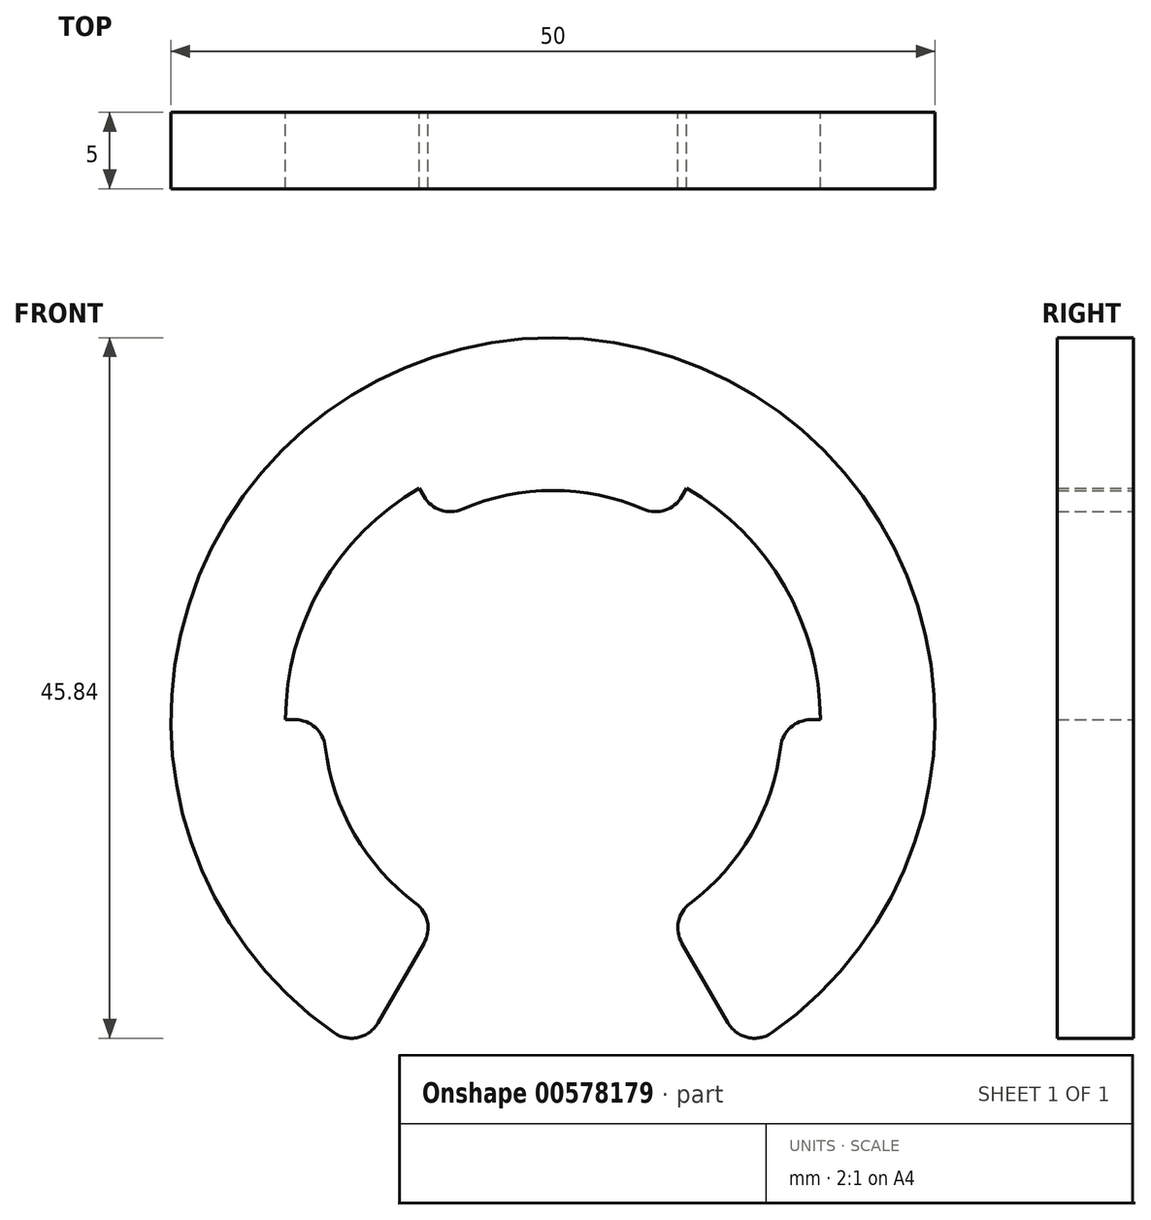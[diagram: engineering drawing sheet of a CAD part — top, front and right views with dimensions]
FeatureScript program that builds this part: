
annotation { "Feature Type Name" : "Feature", "Feature Type Description" : "" }
export const myFeature = defineFeature(function(context is Context, id is Id, definition is map)
    precondition{}
    {
        {
            var Q0;
            Q0=qCreatedBy(makeId("Front.planeOp"),FACE);
            var sketch = newSketch(context, id + "F0", { "sketchPlane" : qUnion([Q0])});
            skArc(sketch, "E0", {"start": v(12.5, -21.65) * mm, "mid": v(0, 25) * mm, "end": v(-12.5, -21.65) * mm});
            skArc(sketch, "E1", {"start": v(8.75, -15.16) * mm, "mid": v(0, 17.5) * mm, "end": v(-8.75, -15.16) * mm});
            skLineSegment(sketch, "E2", {"start": v(7.5, 13) * mm, "end": v(12.5, 21.65) * mm});
            skLineSegment(sketch, "E3", {"start": v(-7.5, 13) * mm, "end": v(-12.5, 21.65) * mm});
            skLineSegment(sketch, "E4", {"start": v(-15, 0) * mm, "end": v(-25, 0) * mm});
            skLineSegment(sketch, "E5", {"start": v(15, 0) * mm, "end": v(25, 0) * mm});
            skLineSegment(sketch, "E6", {"start": v(7.5, -13) * mm, "end": v(12.5, -21.65) * mm});
            skLineSegment(sketch, "E7", {"start": v(-7.5, -13) * mm, "end": v(-12.5, -21.65) * mm});
            skArc(sketch, "E8", {"start": v(7.5, -13) * mm, "mid": v(13, -7.5) * mm, "end": v(15, 0) * mm});
            skArc(sketch, "E9.trimOffspring", {"start": v(-15, 0) * mm, "mid": v(-13, -7.5) * mm, "end": v(-7.5, -13) * mm});
            skArc(sketch, "E10.trimOffspring", {"start": v(7.5, 13) * mm, "mid": v(0, 15) * mm, "end": v(-7.5, 13) * mm});
            skSolve(sketch);
        }
        {
            var Q0;
            {var subQ0=sQuery(id+"F0.wireOp",EDGE,"E3");var subQ1=sQuery(id+"F0.wireOp",EDGE,"E0");var subQ2=makeQuery(id+"F0.imprint","INTERSECT",VERTEX,{"derivedFrom":[subQ1,subQ0]});Q0=makeQuery(id+"F0.imprint","IMPRINT",FACE,{"disambiguationData":[TD([[makeQuery(id+"F0.imprint","IMPRINT",EDGE,{"disambiguationData":[TD([[subQ2,-1.0]])],"derivedFrom":subQ1}),1.0]])]});}
            var Q1;
            {var subQ0=sQuery(id+"F0.wireOp",EDGE,"E7");var subQ1=sQuery(id+"F0.wireOp",EDGE,"E0");var subQ2=makeQuery(id+"F0.imprint","INTERSECT",VERTEX,{"derivedFrom":[subQ1,subQ0]});Q1=makeQuery(id+"F0.imprint","IMPRINT",FACE,{"disambiguationData":[TD([[makeQuery(id+"F0.imprint","IMPRINT",EDGE,{"disambiguationData":[TD([[subQ2,1.0]])],"derivedFrom":subQ1}),1.0]])]});}
            var Q2;
            {var subQ5=sQuery(id+"F0.wireOp",EDGE,"E9.trimOffspring");Q2=makeQuery(id+"F0.imprint","IMPRINT",FACE,{"disambiguationData":[TD([[makeQuery(id+"F0.imprint","IMPRINT",EDGE,{"derivedFrom":subQ5}),-1.0]])]});}
            var Q3;
            {var subQ5=sQuery(id+"F0.wireOp",EDGE,"E10.trimOffspring");Q3=makeQuery(id+"F0.imprint","IMPRINT",FACE,{"disambiguationData":[TD([[makeQuery(id+"F0.imprint","IMPRINT",EDGE,{"derivedFrom":subQ5}),-1.0]])]});}
            var Q4;
            {var subQ0=sQuery(id+"F0.wireOp",EDGE,"E2");var subQ1=sQuery(id+"F0.wireOp",EDGE,"E0");var subQ2=makeQuery(id+"F0.imprint","INTERSECT",VERTEX,{"derivedFrom":[subQ1,subQ0]});Q4=makeQuery(id+"F0.imprint","IMPRINT",FACE,{"disambiguationData":[TD([[makeQuery(id+"F0.imprint","IMPRINT",EDGE,{"disambiguationData":[TD([[subQ2,-1.0]])],"derivedFrom":subQ1}),1.0]])]});}
            var Q5;
            {var subQ0=sQuery(id+"F0.wireOp",EDGE,"E2");var subQ1=sQuery(id+"F0.wireOp",EDGE,"E0");var subQ2=makeQuery(id+"F0.imprint","INTERSECT",VERTEX,{"derivedFrom":[subQ1,subQ0]});Q5=makeQuery(id+"F0.imprint","IMPRINT",FACE,{"disambiguationData":[TD([[makeQuery(id+"F0.imprint","IMPRINT",EDGE,{"disambiguationData":[TD([[subQ2,1.0]])],"derivedFrom":subQ1}),1.0]])]});}
            var Q6;
            {var subQ5=sQuery(id+"F0.wireOp",EDGE,"E8");Q6=makeQuery(id+"F0.imprint","IMPRINT",FACE,{"disambiguationData":[TD([[makeQuery(id+"F0.imprint","IMPRINT",EDGE,{"derivedFrom":subQ5}),-1.0]])]});}
            var Q7;
            {var subQ0=sQuery(id+"F0.wireOp",EDGE,"E6");var subQ1=sQuery(id+"F0.wireOp",EDGE,"E0");var subQ2=makeQuery(id+"F0.imprint","INTERSECT",VERTEX,{"derivedFrom":[subQ1,subQ0]});Q7=makeQuery(id+"F0.imprint","IMPRINT",FACE,{"disambiguationData":[TD([[makeQuery(id+"F0.imprint","IMPRINT",EDGE,{"disambiguationData":[TD([[subQ2,-1.0]])],"derivedFrom":subQ1}),1.0]])]});}
            extrude(context, id + "F1", {"entities" : qUnion([Q0, Q1, Q2, Q3, Q4, Q5, Q6, Q7]), "depth" : 5 * mm, "offsetDistance" : 25 * mm});
        }
        {
            var Q0;
            Q0=makeQuery(id+"F1.opExtrude","SWEPT_EDGE",EDGE,{"disambiguationData":[OSD([sQuery(id+"F0.wireOp",EDGE,"E2"),sQuery(id+"F0.wireOp",EDGE,"E10.trimOffspring")])]});
            var Q1;
            Q1=makeQuery(id+"F1.opExtrude","SWEPT_EDGE",EDGE,{"disambiguationData":[OSD([sQuery(id+"F0.wireOp",EDGE,"E3"),sQuery(id+"F0.wireOp",EDGE,"E10.trimOffspring")])]});
            var Q2;
            Q2=makeQuery(id+"F1.opExtrude","SWEPT_EDGE",EDGE,{"disambiguationData":[OSD([sQuery(id+"F0.wireOp",EDGE,"E4"),sQuery(id+"F0.wireOp",EDGE,"E9.trimOffspring")])]});
            var Q3;
            Q3=makeQuery(id+"F1.opExtrude","SWEPT_EDGE",EDGE,{"disambiguationData":[OSD([sQuery(id+"F0.wireOp",EDGE,"E7"),sQuery(id+"F0.wireOp",EDGE,"E9.trimOffspring")])]});
            var Q4;
            Q4=makeQuery(id+"F1.opExtrude","SWEPT_EDGE",EDGE,{"disambiguationData":[OSD([sQuery(id+"F0.wireOp",EDGE,"E6"),sQuery(id+"F0.wireOp",EDGE,"E8")])]});
            var Q5;
            Q5=makeQuery(id+"F1.opExtrude","SWEPT_EDGE",EDGE,{"disambiguationData":[OSD([sQuery(id+"F0.wireOp",EDGE,"E5"),sQuery(id+"F0.wireOp",EDGE,"E8")])]});
            var Q6;
            Q6=makeQuery(id+"F1.opExtrude","SWEPT_EDGE",EDGE,{"disambiguationData":[OSD([sQuery(id+"F0.wireOp",EDGE,"E0"),sQuery(id+"F0.wireOp",EDGE,"E7")])]});
            var Q7;
            Q7=makeQuery(id+"F1.opExtrude","SWEPT_EDGE",EDGE,{"disambiguationData":[OSD([sQuery(id+"F0.wireOp",EDGE,"E0"),sQuery(id+"F0.wireOp",EDGE,"E6")])]});
            fillet(context, id + "F2", {"entities" : qUnion([Q0, Q1, Q2, Q3, Q4, Q5, Q6, Q7]), "radius" : 2 * mm, "tangentPropagation" : true, "allowEdgeOverflow" : false});
        }
    });
